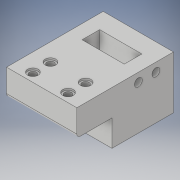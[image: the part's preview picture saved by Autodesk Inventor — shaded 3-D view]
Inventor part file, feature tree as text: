
AUTODESK INVENTOR PART (.ipt)
format: ipt  version: 2019 (Build 230136000, 136)  size: 211,968 bytes
history: native  units: mm
features: sketch x10, extrude x5, hole x5, fillet x1, mirror x1
ambient origin geometry x8: Origin, YZ Plane, XZ Plane, XY Plane, X Axis, Y Axis, Z Axis, Center Point
bodies: Solid1 (feature_tree)
feature tree (22):
  extrude  "Extrusion1"  Depth=20.0mm
  hole  "Hole1"  [1 undecoded]
  fillet  "Fillet1"  Radius=2.0mm
  extrude  "Extrusion2"  Depth=30.0mm
  extrude  "Extrusion3"  Depth=10.0mm TaperAngle=0.0deg
  hole  "Hole2"  [1 undecoded]
  hole  "Hole3"  [1 undecoded]
  extrude  "Extrusion4"  Depth=10.0mm
  extrude  "Extrusion5"  Depth=20.0mm
  hole  "Hole4"  [1 undecoded]
  hole  "Hole5"  [1 undecoded]
  mirror  "Mirror1"
  sketch  "Sketch1"  dims[d0=40.0mm d1=20.0mm]
  sketch  "Sketch2"  dims[d2=15.0mm d3=0.0mm d4=20.0mm]
  sketch  "Sketch3"  dims[d5=4.0mm d6=6.0mm d7=6.0mm d8=1.0mm d9=90.0deg d10=8.0mm d11=20.594885mm d12=2.0mm]
  sketch  "Sketch4"  dims[d13=5.0mm d14=30.0mm]
  sketch  "Sketch5"  dims[d15=15.0mm d16=0.0mm d17=10.0mm d18=0.0mm]
  sketch  "Sketch6"  dims[d19=7.5mm d20=6.0mm d21=8.4mm d22=2.3mm d23=90.0deg d24=10.0mm d25=0.0mm]
  sketch  "Sketch7"  dims[d26=20.0mm d27=6.0mm d28=8.4mm d29=2.3mm d30=90.0deg d31=6.5mm d32=0.0mm d33=8.0mm]
  sketch  "Sketch8"  dims[d34=10.0mm d35=0.0mm d36=10.0mm d37=0.0mm]
  sketch  "Sketch9"  dims[d38=7.5mm d39=6.0mm d40=19.5mm d41=6.0mm d42=90.0deg d43=6.5mm d44=0.0mm d45=10.0mm]
  sketch  "Sketch10"  dims[d46=5.0mm d47=20.0mm d48=3.5mm d49=6.0mm d50=4.5mm d51=6.0mm d52=90.0deg d53=7.0mm d54=0.0mm]
note: 5 required parameter values undecoded (feature->parameter linkage not recoverable at this tier; creation-order binding heuristic only, values carry confidence <= 0.55)
